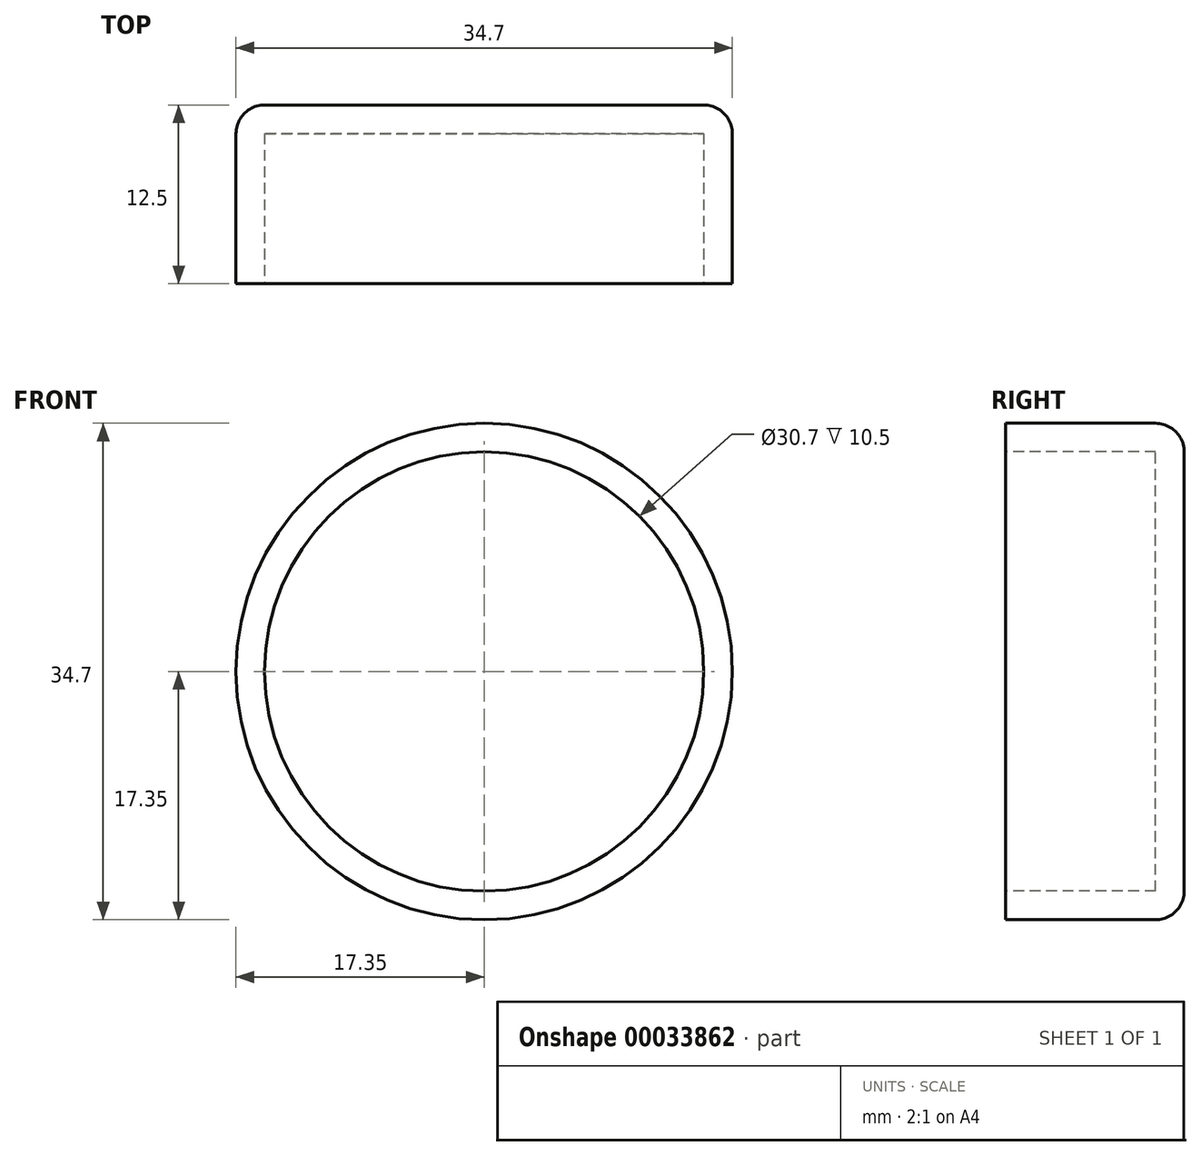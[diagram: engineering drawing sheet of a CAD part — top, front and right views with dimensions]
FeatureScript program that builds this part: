
annotation { "Feature Type Name" : "Feature", "Feature Type Description" : "" }
export const myFeature = defineFeature(function(context is Context, id is Id, definition is map)
    precondition{}
    {
        {
            var Q0;
            Q0=qCreatedBy(makeId("Top.planeOp"),FACE);
            var sketch = newSketch(context, id + "F0", { "sketchPlane" : qUnion([Q0])});
            skLineSegment(sketch, "E0.bottom", {"start": v(0, 0) * mm, "end": v(17.35, 0) * mm, "construction": true});
            skLineSegment(sketch, "E0.top", {"start": v(0, 12.5) * mm, "end": v(17.35, 12.5) * mm, "construction": true});
            skLineSegment(sketch, "E0.left", {"start": v(0, 0) * mm, "end": v(0, 12.5) * mm, "construction": true});
            skLineSegment(sketch, "E0.right", {"start": v(17.35, 0) * mm, "end": v(17.35, 12.5) * mm, "construction": true});
            skLineSegment(sketch, "E1", {"start": v(0, 12.5) * mm, "end": v(17.35, 12.5) * mm});
            skLineSegment(sketch, "E2", {"start": v(17.35, 0) * mm, "end": v(17.35, 12.5) * mm});
            skLineSegment(sketch, "E3.0", {"start": v(15.35, 0) * mm, "end": v(15.35, 10.5) * mm});
            skLineSegment(sketch, "E3.1", {"start": v(0, 10.5) * mm, "end": v(15.35, 10.5) * mm});
            skLineSegment(sketch, "E4", {"start": v(0, 10.5) * mm, "end": v(0, 12.5) * mm});
            skLineSegment(sketch, "E5", {"start": v(15.35, 0) * mm, "end": v(17.35, 0) * mm});
            skSolve(sketch);
        }
        {
            var Q0;
            Q0=qSketchRegion(id+"F0",true);
            var Q1;
            Q1=sQuery(id+"F0.wireOp",EDGE,"E0.left");
            revolve(context, id + "F1", {"entities" : qUnion([Q0]), "axis" : qUnion([Q1]), "revolveType" : RevolveType.FULL});
        }
        {
            var Q0;
            Q0=makeQuery(id+"F1.opRevolve","SWEPT_EDGE",EDGE,{"disambiguationData":[OSD([sQuery(id+"F0.wireOp",EDGE,"E1"),sQuery(id+"F0.wireOp",EDGE,"E2")])]});
            fillet(context, id + "F2", {"entities" : qUnion([Q0]), "radius" : 2 * mm, "tangentPropagation" : true, "allowEdgeOverflow" : false});
        }
    });
